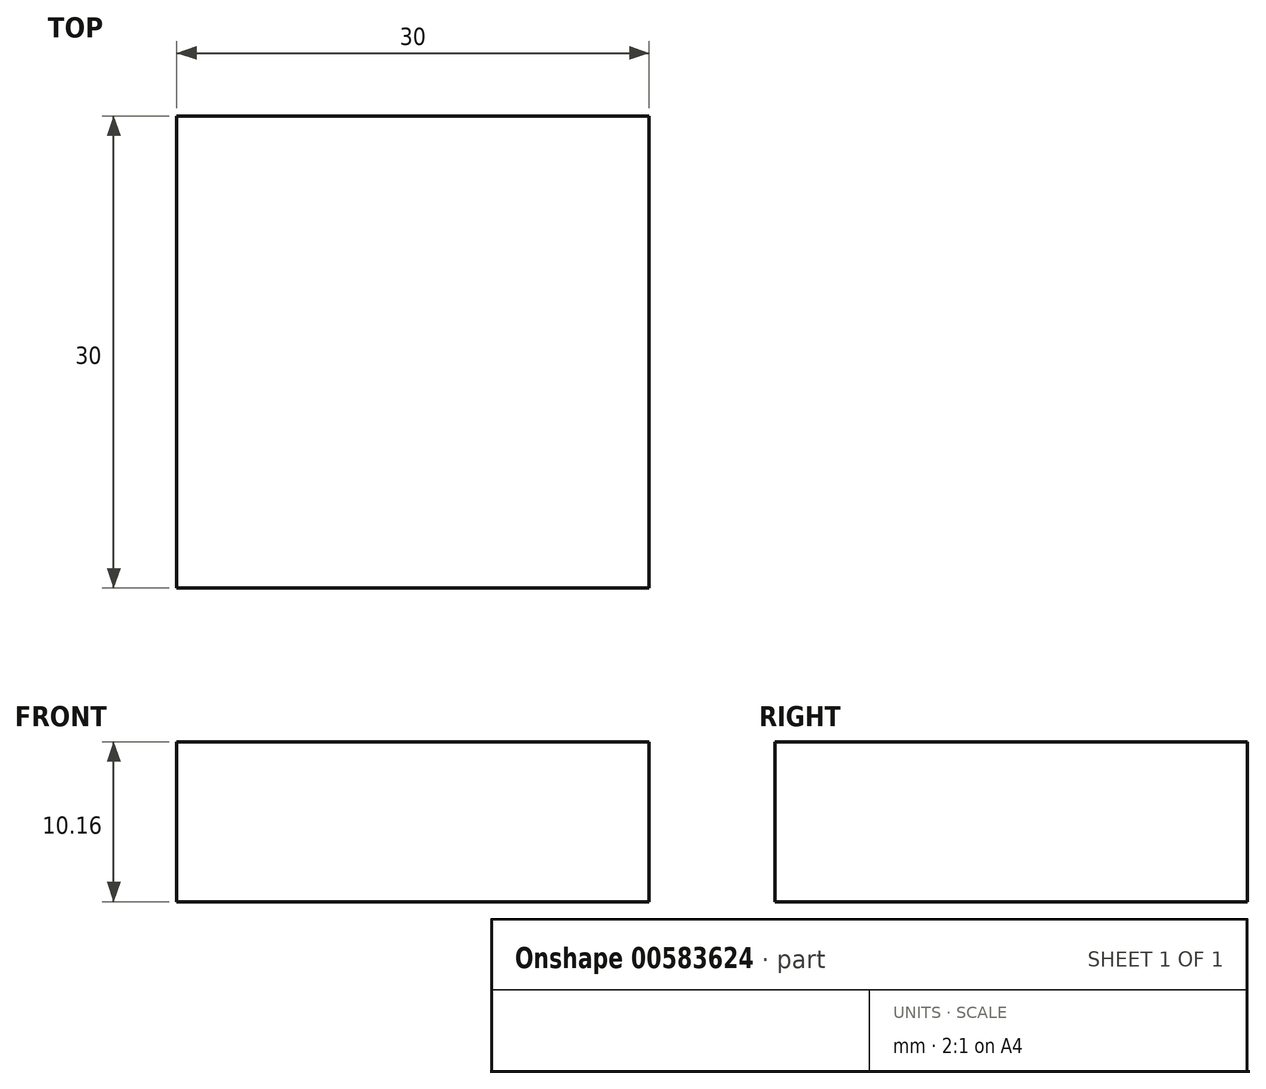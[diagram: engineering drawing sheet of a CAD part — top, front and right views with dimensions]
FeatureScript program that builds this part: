
annotation { "Feature Type Name" : "Feature", "Feature Type Description" : "" }
export const myFeature = defineFeature(function(context is Context, id is Id, definition is map)
    precondition{}
    {
        {
            var Q0;
            Q0=qCreatedBy(makeId("Top.planeOp"),FACE);
            var sketch = newSketch(context, id + "F0", { "sketchPlane" : qUnion([Q0])});
            skLineSegment(sketch, "E0.bottom", {"start": v(15, -15) * mm, "end": v(-15, -15) * mm});
            skLineSegment(sketch, "E0.top", {"start": v(15, 15) * mm, "end": v(-15, 15) * mm});
            skLineSegment(sketch, "E0.left", {"start": v(15, -15) * mm, "end": v(15, 15) * mm});
            skLineSegment(sketch, "E0.right", {"start": v(-15, -15) * mm, "end": v(-15, 15) * mm});
            skPoint(sketch, "E0.middle", {"position": v(0, 0) * mm});
            skSolve(sketch);
        }
        {
            var Q0;
            Q0=makeQuery(id+"F0.imprint","IMPRINT",FACE,{"disambiguationData":[TD([[makeQuery(id+"F0.imprint","IMPRINT",EDGE,{"derivedFrom":sQuery(id+"F0.wireOp",EDGE,"E0.bottom")}),-1.0]])]});
            extrude(context, id + "F1", {"entities" : qUnion([Q0]), "depth" : 10.16 * mm, "offsetDistance" : 25.4 * mm});
        }
        {
            var Q0;
            Q0=makeQuery(id+"F1.opExtrude","CAP_FACE",FACE,{"disambiguationData":[OSD([sQuery(id+"F0.wireOp",EDGE,"E0.bottom"),sQuery(id+"F0.wireOp",EDGE,"E0.top"),sQuery(id+"F0.wireOp",EDGE,"E0.left"),sQuery(id+"F0.wireOp",EDGE,"E0.right")])],"isStart":false});
            var sketch = newSketch(context, id + "F2", { "sketchPlane" : qUnion([Q0])});
            skLineSegment(sketch, "E1.bottom", {"start": v(-15, 15) * mm, "end": v(-9.74, 15) * mm});
            skLineSegment(sketch, "E1.top", {"start": v(-15, 9.74) * mm, "end": v(-9.74, 9.74) * mm});
            skLineSegment(sketch, "E1.left", {"start": v(-15, 15) * mm, "end": v(-15, 9.74) * mm});
            skLineSegment(sketch, "E1.right", {"start": v(-9.74, 15) * mm, "end": v(-9.74, 9.74) * mm});
            skSolve(sketch);
        }
        {
            var Q0;
            Q0=makeQuery(id+"F1.opExtrude","SWEPT_FACE",FACE,{"disambiguationData":[OSD([sQuery(id+"F0.wireOp",EDGE,"E0.bottom")])]});
            var Q1;
            Q1=makeQuery(id+"FrVOPHYhhWgO82d_1.boolean.opBoolean","MERGE",FACE,{"derivedFrom":[makeQuery(id+"F1.opExtrude","SWEPT_FACE",FACE,{"disambiguationData":[OSD([sQuery(id+"F0.wireOp",EDGE,"E0.top")])]}),makeQuery(id+"FrVOPHYhhWgO82d_1.opExtrude","SWEPT_FACE",FACE,{"disambiguationData":[OSD([sQuery(id+"F2.wireOp",EDGE,"E1.bottom")])]})]});
            cPlane(context, id + "F3", {"entities" : qUnion([Q0, Q1]), "cplaneType" : CPlaneType.MID_PLANE, "offset" : 25.4 * mm, "width" : 152.4 * mm, "height" : 152.4 * mm});
        }
    });
